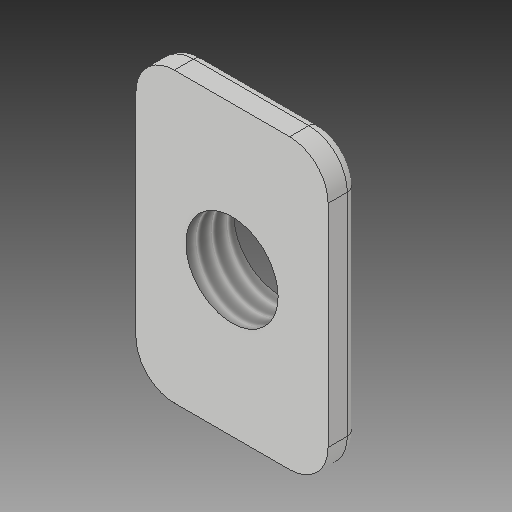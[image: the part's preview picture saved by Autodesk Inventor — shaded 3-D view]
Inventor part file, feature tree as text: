
AUTODESK INVENTOR PART (.ipt)
format: ipt  version: 2017 (Build 210142000, 142)  size: 157,696 bytes
history: native  units: mm
features: other x3, sketch x2
ambient origin geometry x8: Origin, YZ Plane, XZ Plane, XY Plane, X Axis, Y Axis, Z Axis, Center Point
bodies: Solid1 (feature_tree)
feature tree (5):
  other  "M5 Tee Nut-Generic_CPY.ipt"
  other  "Solid1::M5 Tee Nut-Generic_CPY.ipt"
  other  "TaggingFeature1"
  sketch  "Sketch1"  dims[d0=10.0mm]
  sketch  "Sketch2"
